# Revit family: VOGUE PULL-DOWN SINK MIXER
name_source: partatom
category: Specialty Equipment
units: mm (PartAtom-declared; Revit-internal decimal feet)

## family parameters
Cut with Voids When Loaded = No
Host = Face
OmniClass Number = 23.45.55.14
OmniClass Title = Single Faucets
Part Type = Normal
Room Calculation Point = No
Round Connector Dimension = Use Radius
Shared = No

## types (10) — shared parameters
Assembly Code = C1030220
Default Elevation = 1000 mm  [stored 3.28084 ft]
Manufacturer = GWA Bathrooms & Kitchens
Material_Hose = GWA-Plastic-Black
URL = https://www.caroma.com.au

## per-type parameters (varying)
| type | Blade_Handle | Description | Material_Base | Model | Pin_Handle |
| VOGUE PULL-DOWN SINK MIXER CHROME PIN | No | VOGUE PULL-DOWN SINK MIXER CHROME | GWA_Metal-Chrome | 96381C5A | Yes |
| VOGUE PULL-DOWN SINK MIXER MATTE BLACK PIN | No | VOGUE PULL-DOWN SINK MIXER MATTE BLACK | GWA-Metal-Black | 96381B5A | Yes |
| VOGUE PULL-DOWN SINK MIXER GUNMETAL PIN | No | VOGUE PULL-DOWN SINK MIXER GUNMETAL | GWA-Metal-Gunmetal Grey | 96381GM5A | Yes |
| VOGUE PULL-DOWN SINK MIXER BRUSHED NICKEL PIN | No | VOGUE PULL-DOWN SINK MIXER BRUSHED NICKEL | GWA_Metal-Brushed-Nickel | 96381BN5A | Yes |
| VOGUE PULL-DOWN SINK MIXER BRUSHED BRASS PIN | No | VOGUE PULL-DOWN SINK MIXER BRUSHED BRASS | GWA_Metal-Brushed-Brass | 96381BB5A | Yes |
| VOGUE PULL-DOWN SINK MIXER BRUSHED BRASS BLADE | Yes | VOGUE PULL-DOWN SINK MIXER BRUSHED BRASS | GWA_Metal-Brushed-Brass | 96381BB5A | No |
| VOGUE PULL-DOWN SINK MIXER BRUSHED NICKEL BLADE | Yes | VOGUE PULL-DOWN SINK MIXER BRUSHED NICKEL | GWA_Metal-Brushed-Nickel | 96381BN5A | No |
| VOGUE PULL-DOWN SINK MIXER CHROME BLADE | Yes | VOGUE PULL-DOWN SINK MIXER CHROME | GWA_Metal-Chrome | 96381C5A | No |
| VOGUE PULL-DOWN SINK MIXER GUNMETAL BLADE | Yes | VOGUE PULL-DOWN SINK MIXER GUNMETAL | GWA-Metal-Gunmetal Grey | 96381GM5A | No |
| VOGUE PULL-DOWN SINK MIXER MATTE BLACK BLADE | Yes | VOGUE PULL-DOWN SINK MIXER MATTE BLACK | GWA-Metal-Black | 96381B5A | No |

note: [stored X ft] marks values corroborated as IEEE doubles in the binary element streams (Revit-internal decimal feet)

## geometry (parser evidence)
native form markers: Sweep x2
no freeform markers — native parametric forms only
